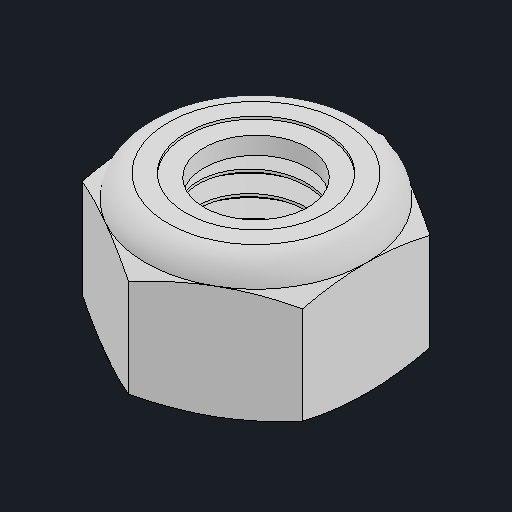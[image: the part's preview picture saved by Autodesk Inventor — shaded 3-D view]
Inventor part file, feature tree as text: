
AUTODESK INVENTOR PART (.ipt)
format: ipt  version: 2024.2 (Build 282272000, 272)  size: 314,368 bytes
history: native  units: mm
features: other x3, revolve x1
ambient origin geometry x8: Origin, YZ Plane, XZ Plane, XY Plane, X Axis, Y Axis, Z Axis, Center Point
bodies: Body1 (feature_tree), Body2 (feature_tree)
feature tree (4):
  other  "솔리드1"
  other  "솔리드2"
  other  "Cut-Revolve4"
  revolve  "Revolve2"  [1 undecoded]
note: 1 required parameter value undecoded (feature->parameter linkage not recoverable at this tier; creation-order binding heuristic only, values carry confidence <= 0.55)
